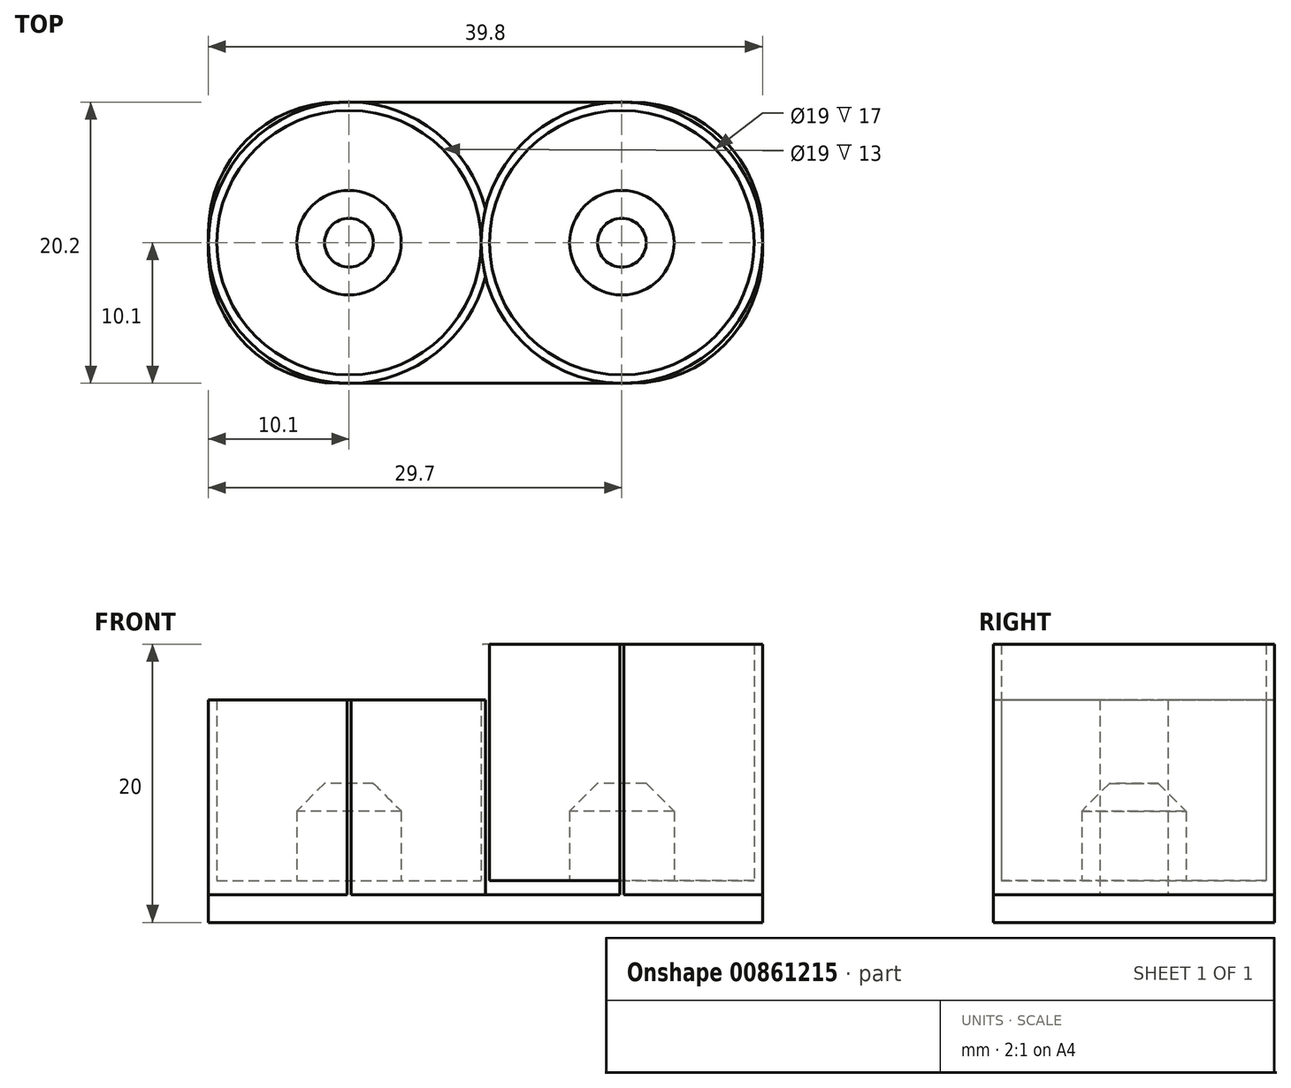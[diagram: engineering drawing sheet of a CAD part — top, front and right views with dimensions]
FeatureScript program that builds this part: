
annotation { "Feature Type Name" : "Feature", "Feature Type Description" : "" }
export const myFeature = defineFeature(function(context is Context, id is Id, definition is map)
    precondition{}
    {
        {
            var Q0;
            Q0=qCreatedBy(makeId("Top.planeOp"),FACE);
            var sketch = newSketch(context, id + "F0", { "sketchPlane" : qUnion([Q0])});
            skLineSegment(sketch, "E0.bottom", {"start": v(0, 10.1) * mm, "end": v(19.9, 10.1) * mm});
            skLineSegment(sketch, "E0.top", {"start": v(0, -10.1) * mm, "end": v(19.9, -10.1) * mm});
            skLineSegment(sketch, "E0.left", {"start": v(0, 10.1) * mm, "end": v(0, -10.1) * mm});
            skLineSegment(sketch, "E0.right", {"start": v(19.9, 10.1) * mm, "end": v(19.9, -10.1) * mm});
            skPoint(sketch, "E1", {"position": v(0, 0) * mm});
            skCircle(sketch, "E2", {"center": v(9.8, 0) * mm, "radius": 9.5 * mm});
            skCircle(sketch, "E3", {"center": v(9.8, 0) * mm, "radius": 3.75 * mm});
            skCircle(sketch, "E4", {"center": v(9.8, 0) * mm, "radius": 10.1 * mm});
            skPoint(sketch, "E5", {"position": v(19.9, 0) * mm});
            skPoint(sketch, "E6", {"position": v(9.95, 10.1) * mm});
            skPoint(sketch, "E7", {"position": v(9.95, -10.1) * mm});
            skSolve(sketch);
        }
        {
            var Q0;
            Q0=makeQuery(id+"F0.imprint","IMPRINT",FACE,{"disambiguationData":[TD([[makeQuery(id+"F0.imprint","IMPRINT",EDGE,{"derivedFrom":sQuery(id+"F0.wireOp",EDGE,"E3")}),1.0]])]});
            extrude(context, id + "F1", {"entities" : qUnion([Q0]), "depth" : 10 * mm, "offsetDistance" : 25 * mm});
        }
        {
            var Q0;
            Q0=makeQuery(id+"F0.imprint","IMPRINT",FACE,{"disambiguationData":[TD([[makeQuery(id+"F0.imprint","IMPRINT",EDGE,{"derivedFrom":sQuery(id+"F0.wireOp",EDGE,"E2")}),1.0]])]});
            extrude(context, id + "F2", {"entities" : qUnion([Q0]), "operationType" : NewBodyOperationType.ADD, "depth" : 3 * mm, "offsetDistance" : 25 * mm});
        }
        {
            var Q0;
            Q0=makeQuery(id+"F0.imprint","IMPRINT",FACE,{"disambiguationData":[TD([[makeQuery(id+"F0.imprint","IMPRINT",EDGE,{"derivedFrom":sQuery(id+"F0.wireOp",EDGE,"E2")}),-1.0]])]});
            var Q1;
            {var subQ0=sQuery(id+"F0.wireOp",EDGE,"E4");var subQ1=sQuery(id+"F0.wireOp",EDGE,"E0.right");var subQ2=makeQuery(id+"F0.imprint","INTERSECT",VERTEX,{"disambiguationData":[OD(0.0)],"derivedFrom":[subQ1,subQ0]});Q1=makeQuery(id+"F0.imprint","IMPRINT",FACE,{"disambiguationData":[TD([[makeQuery(id+"F0.imprint","IMPRINT",EDGE,{"disambiguationData":[TD([[subQ2,-1.0]])],"derivedFrom":subQ1}),1.0]])]});}
            extrude(context, id + "F3", {"entities" : qUnion([Q0, Q1]), "operationType" : NewBodyOperationType.ADD, "depth" : 20 * mm, "offsetDistance" : 25 * mm});
        }
        {
            var Q0;
            Q0=makeQuery(id+"F0.imprint","IMPRINT",FACE,{"disambiguationData":[TD([[makeQuery(id+"F0.imprint","IMPRINT",EDGE,{"derivedFrom":sQuery(id+"F0.wireOp",EDGE,"E0.bottom")}),-1.0]])]});
            var Q1;
            {var subQ0=sQuery(id+"F0.wireOp",EDGE,"E0.top");Q1=makeQuery(id+"F0.imprint","IMPRINT",FACE,{"disambiguationData":[TD([[makeQuery(id+"F0.imprint","IMPRINT",EDGE,{"derivedFrom":subQ0}),1.0]])]});}
            extrude(context, id + "F4", {"entities" : qUnion([Q0, Q1]), "operationType" : NewBodyOperationType.ADD, "depth" : 2 * mm, "offsetDistance" : 25 * mm});
        }
        {
            var Q0;
            Q0=makeQuery(id+"F4.opExtrude","SWEPT_EDGE",EDGE,{"disambiguationData":[OSD([sQuery(id+"F0.wireOp",EDGE,"E0.bottom"),sQuery(id+"F0.wireOp",EDGE,"E0.right")])]});
            var Q1;
            Q1=makeQuery(id+"F4.opExtrude","SWEPT_EDGE",EDGE,{"disambiguationData":[OSD([sQuery(id+"F0.wireOp",EDGE,"E0.top"),sQuery(id+"F0.wireOp",EDGE,"E0.right")])]});
            fillet(context, id + "F5", {"entities" : qUnion([Q0, Q1]), "radius" : 9.35 * mm, "tangentPropagation" : true, "allowEdgeOverflow" : false});
        }
        {
            var Q0;
            Q0=makeQuery(id+"F1.opExtrude","SWEPT_BODY",BODY,{"disambiguationData":[OSD([sQuery(id+"F0.wireOp",EDGE,"E3")])]});
            var Q1;
            Q1=qCreatedBy(makeId("Right.planeOp"),FACE);
            mirror(context, id + "F6", {"operationType" : NewBodyOperationType.ADD, "entities" : qUnion([Q0]), "mirrorPlane" : qUnion([Q1])});
        }
        {
            var Q0;
            {var subQ0=makeQuery(id+"F3.opExtrude","CAP_FACE",FACE,{"disambiguationData":[OSD([sQuery(id+"F0.wireOp",EDGE,"E0.left"),sQuery(id+"F0.wireOp",EDGE,"E2"),sQuery(id+"F0.wireOp",EDGE,"E4")])],"isStart":false});Q0=makeQuery(id+"F6.boolean.opBoolean","MERGE",FACE,{"derivedFrom":[subQ0,makeQuery(id+"F6.opPattern","COPY",FACE,{"derivedFrom":subQ0,"instanceName":"1"})]});}
            var sketch = newSketch(context, id + "F7", { "sketchPlane" : qUnion([Q0])});
            skArc(sketch, "E8", {"start": v(0, 2.44) * mm, "mid": v(-19.9, 0) * mm, "end": v(0, -2.44) * mm});
            skCircle(sketch, "E9.0", {"center": v(-9.8, 0) * mm, "radius": 3.75 * mm, "construction": true});
            skCircle(sketch, "E10.0", {"center": v(9.8, 0) * mm, "radius": 3.75 * mm, "construction": true});
            skArc(sketch, "E11", {"start": v(0, -2.44) * mm, "mid": v(-0.3, 0) * mm, "end": v(0, 2.44) * mm});
            skSolve(sketch);
        }
        {
            var Q0;
            Q0=makeQuery(id+"F7.imprint","IMPRINT",FACE,{"disambiguationData":[TD([[makeQuery(id+"F7.imprint","IMPRINT",EDGE,{"derivedFrom":makeQuery(id+"F6.opPattern","COPY",EDGE,{"derivedFrom":makeQuery(id+"F3.opExtrude","CAP_EDGE",EDGE,{"disambiguationData":[OSD([sQuery(id+"F0.wireOp",EDGE,"E2")])],"isStart":false}),"instanceName":"1"})}),-1.0]])]});
            var Q1;
            {var subQ8=sQuery(id+"F0.wireOp",EDGE,"E0.bottom");var subQ9=makeQuery(id+"F6.opPattern","COPY",EDGE,{"derivedFrom":makeQuery(id+"F3.opExtrude","CAP_EDGE",EDGE,{"disambiguationData":[OSD([subQ8])],"isStart":false}),"instanceName":"1"});Q1=makeQuery(id+"F7.imprint","IMPRINT",FACE,{"disambiguationData":[TD([[makeQuery(id+"F7.imprint","IMPRINT",EDGE,{"derivedFrom":subQ9}),1.0]])]});}
            extrude(context, id + "F8", {"entities" : qUnion([Q0, Q1]), "operationType" : NewBodyOperationType.REMOVE, "oppositeDirection" : true, "depth" : 4 * mm, "offsetDistance" : 25 * mm});
        }
        {
            var Q0;
            Q0=makeQuery(id+"F8.boolean.opBoolean","COPY",FACE,{"derivedFrom":makeQuery(id+"F8.opExtrude","CAP_FACE",FACE,{"disambiguationData":[OSD([sQuery(id+"F0.wireOp",EDGE,"E3")])],"isStart":false})});
            var Q1;
            Q1=makeQuery(id+"F1.opExtrude","CAP_FACE",FACE,{"disambiguationData":[OSD([sQuery(id+"F0.wireOp",EDGE,"E3")])],"isStart":false});
            var Q2;
            Q2=makeQuery(id+"F6.opPattern","COPY",FACE,{"derivedFrom":makeQuery(id+"F1.opExtrude","CAP_FACE",FACE,{"disambiguationData":[OSD([sQuery(id+"F0.wireOp",EDGE,"E3")])],"isStart":false}),"instanceName":"1"});
            chamfer(context, id + "F9", {"entities" : qUnion([Q0, Q1, Q2]), "width" : 2 * mm, "tangentPropagation" : true});
        }
    });
